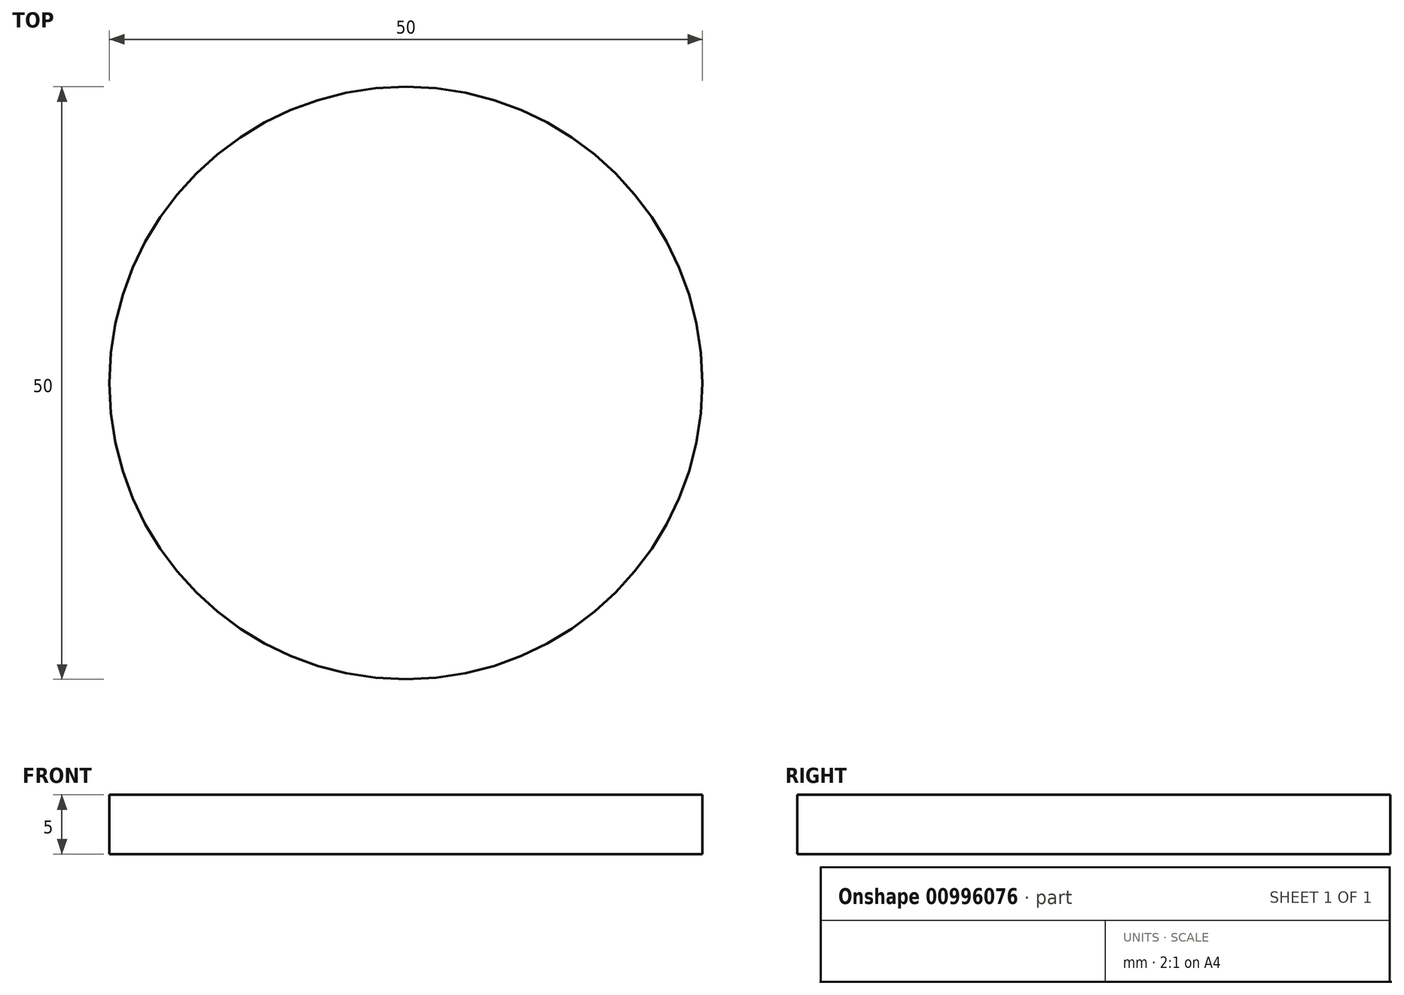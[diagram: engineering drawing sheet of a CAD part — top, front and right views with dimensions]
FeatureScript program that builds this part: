
annotation { "Feature Type Name" : "Feature", "Feature Type Description" : "" }
export const myFeature = defineFeature(function(context is Context, id is Id, definition is map)
    precondition{}
    {
        {
            var Q0;
            Q0=qCreatedBy(makeId("Top.planeOp"),FACE);
            var sketch = newSketch(context, id + "F0", { "sketchPlane" : qUnion([Q0])});
            skCircle(sketch, "E0", {"center": v(0, 0) * mm, "radius": 25 * mm});
            skSolve(sketch);
        }
        {
            var Q0;
            Q0=qSketchRegion(id+"F0",true);
            extrude(context, id + "F1", {"entities" : qUnion([Q0]), "depth" : 5 * mm, "offsetDistance" : 25 * mm});
        }
    });
